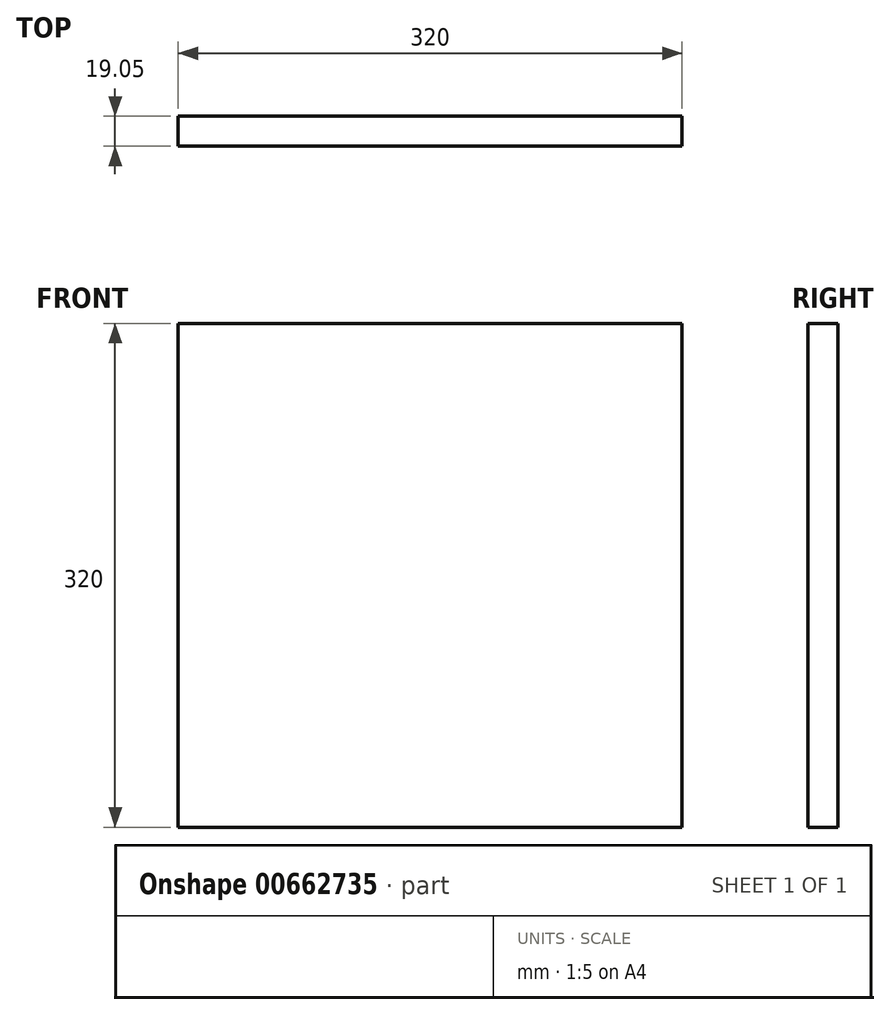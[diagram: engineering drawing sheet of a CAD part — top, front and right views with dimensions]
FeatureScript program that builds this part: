
annotation { "Feature Type Name" : "Feature", "Feature Type Description" : "" }
export const myFeature = defineFeature(function(context is Context, id is Id, definition is map)
    precondition{}
    {
        {
            var Q0;
            Q0=qCreatedBy(makeId("Front.planeOp"),FACE);
            var sketch = newSketch(context, id + "F0", { "sketchPlane" : qUnion([Q0])});
            skLineSegment(sketch, "E0.bottom", {"start": v(160, 160) * mm, "end": v(-160, 160) * mm});
            skLineSegment(sketch, "E0.top", {"start": v(160, -160) * mm, "end": v(-160, -160) * mm});
            skLineSegment(sketch, "E0.left", {"start": v(160, 160) * mm, "end": v(160, -160) * mm});
            skLineSegment(sketch, "E0.right", {"start": v(-160, 160) * mm, "end": v(-160, -160) * mm});
            skPoint(sketch, "E0.middle", {"position": v(0, 0) * mm});
            skSolve(sketch);
        }
        {
            var Q0;
            Q0=makeQuery(id+"F0.imprint","IMPRINT",FACE,{"disambiguationData":[TD([[makeQuery(id+"F0.imprint","IMPRINT",EDGE,{"derivedFrom":sQuery(id+"F0.wireOp",EDGE,"E0.bottom")}),1.0]])]});
            extrude(context, id + "F1", {"entities" : qUnion([Q0]), "depth" : (25.4 * .75) * mm, "offsetDistance" : 25 * mm});
        }
    });
